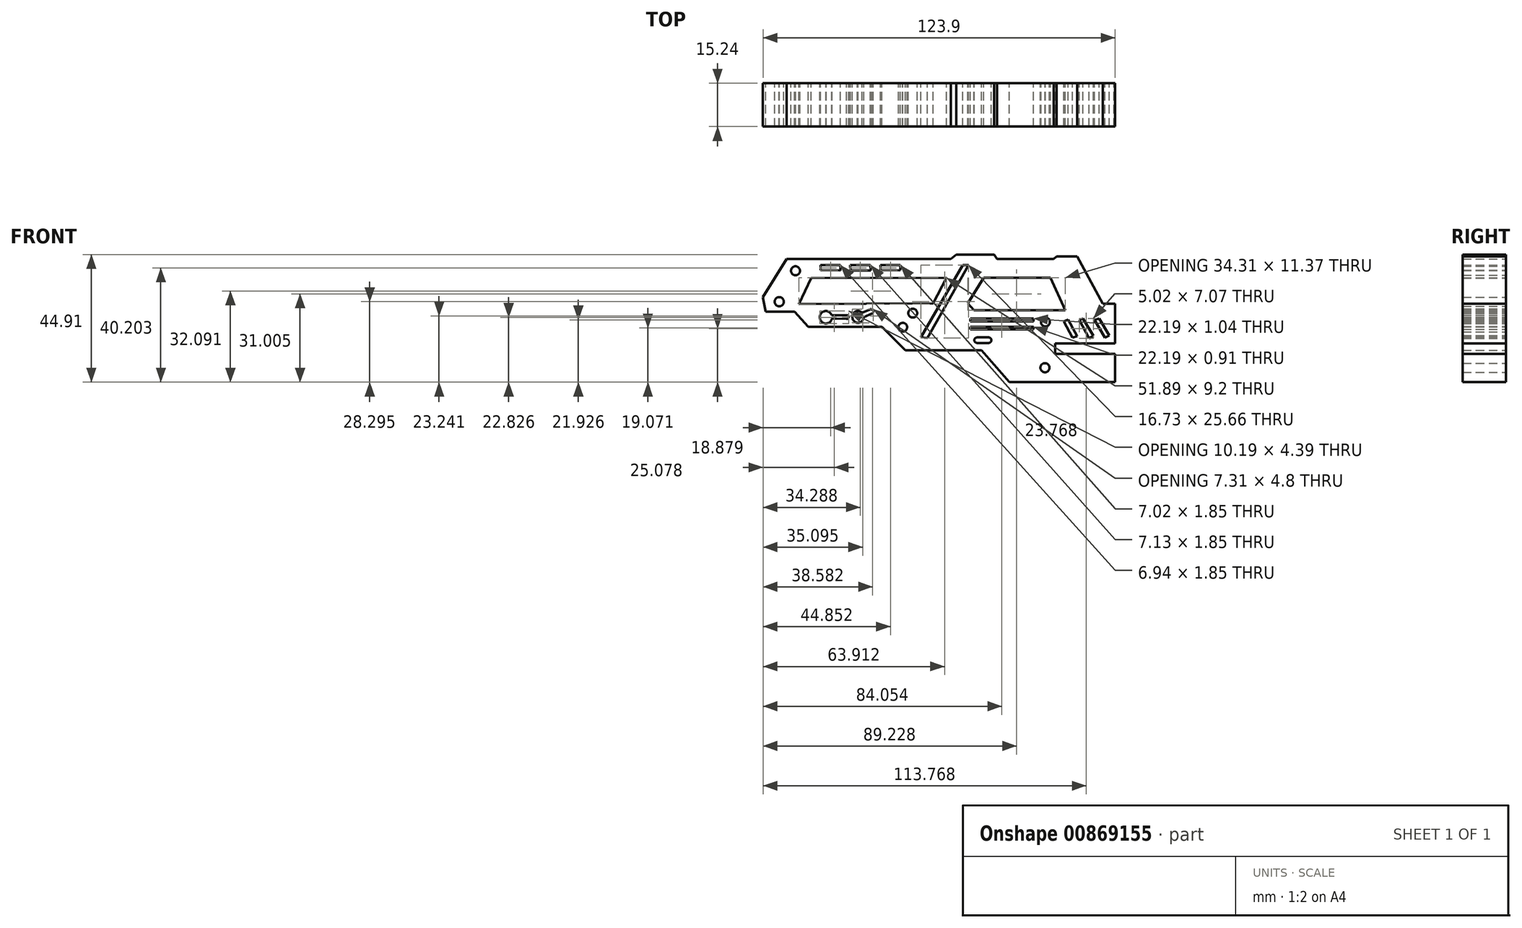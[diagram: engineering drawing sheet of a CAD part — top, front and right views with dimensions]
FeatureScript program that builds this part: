
annotation { "Feature Type Name" : "Feature", "Feature Type Description" : "" }
export const myFeature = defineFeature(function(context is Context, id is Id, definition is map)
    precondition{}
    {
        {
            var Q0;
            Q0=qCreatedBy(makeId("Front.planeOp"),FACE);
            var sketch = newSketch(context, id + "F0", { "sketchPlane" : qUnion([Q0])});
            skLineSegment(sketch, "E0", {"start": v(-62.2, 26.43) * mm, "end": v(-53.9, 39.85) * mm});
            skLineSegment(sketch, "E1", {"start": v(-53.9, 39.85) * mm, "end": v(3.91, 39.85) * mm});
            skLineSegment(sketch, "E2", {"start": v(3.91, 39.85) * mm, "end": v(5.84, 41.45) * mm});
            skLineSegment(sketch, "E3", {"start": v(5.84, 41.45) * mm, "end": v(19.17, 41.45) * mm});
            skLineSegment(sketch, "E4", {"start": v(19.17, 41.45) * mm, "end": v(20.2, 39.85) * mm});
            skLineSegment(sketch, "E5", {"start": v(20.2, 39.85) * mm, "end": v(40.17, 39.85) * mm});
            skLineSegment(sketch, "E6", {"start": v(40.17, 39.85) * mm, "end": v(41.14, 40.8) * mm});
            skLineSegment(sketch, "E7", {"start": v(41.14, 40.8) * mm, "end": v(48.3, 40.8) * mm});
            skLineSegment(sketch, "E8", {"start": v(48.3, 40.8) * mm, "end": v(57.4, 24.1) * mm});
            skLineSegment(sketch, "E9", {"start": v(61.7, 21.4) * mm, "end": v(61.7, 17.16) * mm});
            skLineSegment(sketch, "E10", {"start": v(61.7, 14.01) * mm, "end": v(61.7, 10.1) * mm});
            skLineSegment(sketch, "E11", {"start": v(61.7, 10.1) * mm, "end": v(31.32, 10.1) * mm});
            skArc(sketch, "E12", {"start": v(31.32, 10.1) * mm, "mid": v(29.48, 8.26) * mm, "end": v(31.32, 6.43) * mm});
            skLineSegment(sketch, "E13", {"start": v(31.32, 6.43) * mm, "end": v(61.34, 6.43) * mm});
            skLineSegment(sketch, "E14", {"start": v(61.34, 6.43) * mm, "end": v(61.34, 3.6) * mm});
            skLineSegment(sketch, "E15", {"start": v(61.7, 0) * mm, "end": v(61.7, -3.46) * mm});
            skLineSegment(sketch, "E16", {"start": v(61.7, -3.46) * mm, "end": v(24.42, -3.46) * mm});
            skLineSegment(sketch, "E17", {"start": v(24.42, -3.46) * mm, "end": v(14.7, 7.79) * mm});
            skLineSegment(sketch, "E18", {"start": v(14.7, 7.79) * mm, "end": v(-12.14, 7.79) * mm});
            skLineSegment(sketch, "E19", {"start": v(-12.14, 7.79) * mm, "end": v(-20.36, 16) * mm});
            skLineSegment(sketch, "E20", {"start": v(-20.36, 16) * mm, "end": v(-46.21, 16) * mm});
            skLineSegment(sketch, "E21", {"start": v(-46.21, 16) * mm, "end": v(-51.04, 21.3) * mm});
            skLineSegment(sketch, "E22", {"start": v(-51.04, 21.3) * mm, "end": v(-61.25, 21.3) * mm});
            skLineSegment(sketch, "E23", {"start": v(-61.25, 21.3) * mm, "end": v(-62.2, 26.43) * mm});
            skLineSegment(sketch, "E24", {"start": v(12.34, 25.63) * mm, "end": v(15.68, 30.57) * mm});
            skLineSegment(sketch, "E25", {"start": v(15.68, 30.57) * mm, "end": v(37.45, 30.57) * mm});
            skLineSegment(sketch, "E26", {"start": v(37.45, 30.57) * mm, "end": v(40.6, 24.3) * mm});
            skLineSegment(sketch, "E27", {"start": v(40.6, 24.3) * mm, "end": v(13.46, 24.3) * mm});
            skLineSegment(sketch, "E28", {"start": v(13.46, 24.3) * mm, "end": v(12.34, 25.63) * mm});
            skPoint(sketch, "E29.start.orphan", {"position": v(-49.56, 26.43) * mm});
            skPoint(sketch, "E30.start.orphan", {"position": v(-46.21, 33.1) * mm});
            skPoint(sketch, "E31.end.orphan", {"position": v(-49.56, 24.03) * mm});
            skLineSegment(sketch, "E32", {"start": v(-45.79, 27.78) * mm, "end": v(-43.34, 31.74) * mm});
            skLineSegment(sketch, "E33", {"start": v(-43.34, 31.74) * mm, "end": v(0, 31.74) * mm});
            skLineSegment(sketch, "E34", {"start": v(0, 31.74) * mm, "end": v(-2.07, 27.18) * mm});
            skLineSegment(sketch, "E35", {"start": v(-2.07, 27.18) * mm, "end": v(-45.79, 27.78) * mm});
            skPoint(sketch, "E36.start.orphan", {"position": v(59.67, 0) * mm});
            skLineSegment(sketch, "E37", {"start": v(61.7, 10.1) * mm, "end": v(61.7, 24.1) * mm});
            skLineSegment(sketch, "E38", {"start": v(61.7, 24.1) * mm, "end": v(57.4, 24.1) * mm});
            skLineSegment(sketch, "E39", {"start": v(57.4, 24.1) * mm, "end": v(61.7, 24.1) * mm});
            skLineSegment(sketch, "E40", {"start": v(-6.65, 12.26) * mm, "end": v(8.03, 37.67) * mm});
            skLineSegment(sketch, "E41", {"start": v(8.03, 37.67) * mm, "end": v(10.07, 37.67) * mm});
            skLineSegment(sketch, "E42", {"start": v(10.07, 37.67) * mm, "end": v(-4.35, 12) * mm});
            skLineSegment(sketch, "E43", {"start": v(-4.35, 12) * mm, "end": v(-6.65, 12.26) * mm});
            skLineSegment(sketch, "E44", {"start": v(-1.93, 12.26) * mm, "end": v(12.36, 37.67) * mm});
            skLineSegment(sketch, "E45", {"start": v(12.36, 37.67) * mm, "end": v(14.29, 37.67) * mm});
            skLineSegment(sketch, "E46", {"start": v(14.29, 37.67) * mm, "end": v(-0.14, 12) * mm});
            skLineSegment(sketch, "E47", {"start": v(-0.14, 12) * mm, "end": v(-1.96, 12.03) * mm});
            skLineSegment(sketch, "E48", {"start": v(10.76, 18.92) * mm, "end": v(10.76, 17.95) * mm});
            skLineSegment(sketch, "E49", {"start": v(10.76, 17.95) * mm, "end": v(32.95, 17.95) * mm});
            skLineSegment(sketch, "E50", {"start": v(32.95, 17.95) * mm, "end": v(32.95, 18.98) * mm});
            skLineSegment(sketch, "E51", {"start": v(32.95, 18.98) * mm, "end": v(10.76, 18.92) * mm});
            skLineSegment(sketch, "E52", {"start": v(10.76, 15.16) * mm, "end": v(32.95, 15.16) * mm});
            skLineSegment(sketch, "E53", {"start": v(32.95, 15.16) * mm, "end": v(32.95, 16.06) * mm});
            skLineSegment(sketch, "E54", {"start": v(32.95, 16.06) * mm, "end": v(10.76, 16.06) * mm});
            skLineSegment(sketch, "E55", {"start": v(10.76, 16.06) * mm, "end": v(10.76, 15.16) * mm});
            skLineSegment(sketch, "E56", {"start": v(35.6, 2.11) * mm, "end": v(35.6, 2.32) * mm});
            skLineSegment(sketch, "E57", {"start": v(-13.26, 8.9) * mm, "end": v(-4.35, 24.3) * mm});
            skLineSegment(sketch, "E58", {"start": v(-4.35, 24.3) * mm, "end": v(-2.07, 26.59) * mm});
            skLineSegment(sketch, "E59", {"start": v(40.6, -3.46) * mm, "end": v(40.6, 20.92) * mm});
            skLineSegment(sketch, "E60", {"start": v(40.6, 20.92) * mm, "end": v(39, 24.1) * mm});
            skLineSegment(sketch, "E61", {"start": v(28.58, 30.57) * mm, "end": v(28.58, 39.85) * mm});
            skLineSegment(sketch, "E62", {"start": v(1.26, 31.74) * mm, "end": v(1.26, 33.23) * mm});
            skLineSegment(sketch, "E63", {"start": v(1.26, 33.23) * mm, "end": v(5.08, 39.85) * mm});
            skLineSegment(sketch, "E64", {"start": v(5.08, 39.85) * mm, "end": v(5.84, 41.45) * mm});
            skLineSegment(sketch, "E65", {"start": v(-49.56, 24.03) * mm, "end": v(-2.3, 24.3) * mm});
            skLineSegment(sketch, "E66", {"start": v(-2.3, 24.3) * mm, "end": v(2.33, 33.23) * mm});
            skLineSegment(sketch, "E67", {"start": v(2.33, 33.23) * mm, "end": v(-45.19, 33.1) * mm});
            skLineSegment(sketch, "E68", {"start": v(-45.19, 33.1) * mm, "end": v(-49.56, 24.03) * mm});
            skLineSegment(sketch, "E69", {"start": v(9.87, 24.3) * mm, "end": v(11.98, 21.86) * mm});
            skLineSegment(sketch, "E70", {"start": v(11.98, 21.86) * mm, "end": v(44.18, 21.86) * mm});
            skLineSegment(sketch, "E71", {"start": v(44.18, 21.86) * mm, "end": v(39, 33.23) * mm});
            skLineSegment(sketch, "E72", {"start": v(39, 33.23) * mm, "end": v(15.47, 33.23) * mm});
            skLineSegment(sketch, "E73", {"start": v(15.47, 33.23) * mm, "end": v(9.87, 24.3) * mm});
            skLineSegment(sketch, "E74", {"start": v(-41.9, 35.92) * mm, "end": v(-41.9, 37.67) * mm});
            skLineSegment(sketch, "E75", {"start": v(-41.9, 37.67) * mm, "end": v(-34.97, 37.67) * mm});
            skLineSegment(sketch, "E76", {"start": v(-34.97, 37.67) * mm, "end": v(-34.96, 35.82) * mm});
            skLineSegment(sketch, "E77", {"start": v(-34.96, 35.82) * mm, "end": v(-41.9, 35.92) * mm});
            skLineSegment(sketch, "E78", {"start": v(-31.47, 35.82) * mm, "end": v(-31.48, 37.67) * mm});
            skLineSegment(sketch, "E79", {"start": v(-31.48, 37.67) * mm, "end": v(-24.36, 37.67) * mm});
            skLineSegment(sketch, "E80", {"start": v(-24.36, 37.67) * mm, "end": v(-24.35, 35.82) * mm});
            skLineSegment(sketch, "E81", {"start": v(-24.35, 35.82) * mm, "end": v(-31.47, 35.82) * mm});
            skLineSegment(sketch, "E82", {"start": v(-20.85, 35.82) * mm, "end": v(-20.86, 37.67) * mm});
            skLineSegment(sketch, "E83", {"start": v(-20.86, 37.67) * mm, "end": v(-13.84, 37.67) * mm});
            skLineSegment(sketch, "E84", {"start": v(-13.84, 37.67) * mm, "end": v(-13.84, 35.92) * mm});
            skLineSegment(sketch, "E85", {"start": v(-13.84, 35.92) * mm, "end": v(-20.85, 35.82) * mm});
            skLineSegment(sketch, "E86", {"start": v(-8.77, 39.85) * mm, "end": v(-8.76, 38.45) * mm});
            skLineSegment(sketch, "E87", {"start": v(-8.76, 38.45) * mm, "end": v(-1.27, 38.45) * mm});
            skLineSegment(sketch, "E88", {"start": v(-1.27, 38.45) * mm, "end": v(-1.28, 39.85) * mm});
            skLineSegment(sketch, "E89", {"start": v(-38, 20.4) * mm, "end": v(-38, 20.03) * mm});
            skPoint(sketch, "E90.start.orphan", {"position": v(-40.9, 21.11) * mm});
            skLineSegment(sketch, "E91", {"start": v(-42.17, 20.03) * mm, "end": v(-32.77, 20.03) * mm});
            skLineSegment(sketch, "E92", {"start": v(-42.16, 19) * mm, "end": v(-32.8, 18.83) * mm});
            skArc(sketch, "E93", {"start": v(-32.8, 18.83) * mm, "mid": v(-32.03, 19.4) * mm, "end": v(-32.77, 20.03) * mm});
            skLineSegment(sketch, "E94", {"start": v(43.6, 17.86) * mm, "end": v(46.74, 12.23) * mm});
            skLineSegment(sketch, "E95", {"start": v(46.74, 12.23) * mm, "end": v(48.4, 12.64) * mm});
            skLineSegment(sketch, "E96", {"start": v(48.4, 12.64) * mm, "end": v(45.12, 18.58) * mm});
            skLineSegment(sketch, "E97", {"start": v(45.12, 18.58) * mm, "end": v(43.6, 17.86) * mm});
            skLineSegment(sketch, "E98", {"start": v(49.06, 18.37) * mm, "end": v(50.38, 18.95) * mm});
            skLineSegment(sketch, "E99", {"start": v(50.38, 18.95) * mm, "end": v(54.08, 12.81) * mm});
            skLineSegment(sketch, "E100", {"start": v(54.08, 12.81) * mm, "end": v(52.54, 11.89) * mm});
            skLineSegment(sketch, "E101", {"start": v(52.54, 11.89) * mm, "end": v(49.06, 18.37) * mm});
            skLineSegment(sketch, "E102", {"start": v(54.44, 18.37) * mm, "end": v(58.18, 12.23) * mm});
            skLineSegment(sketch, "E103", {"start": v(58.18, 12.23) * mm, "end": v(59.7, 12.9) * mm});
            skLineSegment(sketch, "E104", {"start": v(59.7, 12.9) * mm, "end": v(56.15, 18.93) * mm});
            skLineSegment(sketch, "E105", {"start": v(56.15, 18.93) * mm, "end": v(54.44, 18.37) * mm});
            skLineSegment(sketch, "E106", {"start": v(61.6, 13.65) * mm, "end": v(59.95, 13.65) * mm});
            skLineSegment(sketch, "E107", {"start": v(59.95, 13.65) * mm, "end": v(59.93, 17.16) * mm});
            skLineSegment(sketch, "E108", {"start": v(59.93, 17.16) * mm, "end": v(61.7, 17.16) * mm});
            skLineSegment(sketch, "E109", {"start": v(61.7, -0.64) * mm, "end": v(61.7, 6.43) * mm});
            skLineSegment(sketch, "E110", {"start": v(61.7, 6.43) * mm, "end": v(61.34, 6.43) * mm});
            skLineSegment(sketch, "E111", {"start": v(61.7, 3.23) * mm, "end": v(59.7, 3.23) * mm});
            skLineSegment(sketch, "E112", {"start": v(59.7, 3.23) * mm, "end": v(59.72, -0.56) * mm});
            skLineSegment(sketch, "E113", {"start": v(59.72, -0.56) * mm, "end": v(61.7, -0.56) * mm});
            skLineSegment(sketch, "E114", {"start": v(55.3, -1.75) * mm, "end": v(42.91, -1.75) * mm});
            skLineSegment(sketch, "E115", {"start": v(42.91, -1.75) * mm, "end": v(42.91, 4.58) * mm});
            skLineSegment(sketch, "E116", {"start": v(42.91, 4.58) * mm, "end": v(55.3, 4.58) * mm});
            skLineSegment(sketch, "E117", {"start": v(55.3, 4.58) * mm, "end": v(55.3, 4.37) * mm});
            skLineSegment(sketch, "E118", {"start": v(41.14, 33.74) * mm, "end": v(46.43, 23.05) * mm});
            skLineSegment(sketch, "E119", {"start": v(55.78, 23.05) * mm, "end": v(47.72, 37.85) * mm});
            skArc(sketch, "E120", {"start": v(46.1, 33.68) * mm, "mid": v(47.87, 35.39) * mm, "end": v(47.72, 37.85) * mm});
            skLineSegment(sketch, "E121", {"start": v(41.14, 33.74) * mm, "end": v(46.1, 33.68) * mm});
            skLineSegment(sketch, "E122", {"start": v(15.82, 34.57) * mm, "end": v(27.34, 34.44) * mm});
            skLineSegment(sketch, "E123", {"start": v(27.34, 38.3) * mm, "end": v(18, 38.3) * mm});
            skLineSegment(sketch, "E124", {"start": v(18, 38.3) * mm, "end": v(15.82, 34.57) * mm});
            skLineSegment(sketch, "E125", {"start": v(17.21, 10.34) * mm, "end": v(13.11, 10.34) * mm});
            skArc(sketch, "E126", {"start": v(13.11, 12.26) * mm, "mid": v(12.15, 11.3) * mm, "end": v(13.11, 10.34) * mm});
            skLineSegment(sketch, "E127", {"start": v(13.11, 12.26) * mm, "end": v(17.21, 12.26) * mm});
            skArc(sketch, "E128", {"start": v(17.21, 10.34) * mm, "mid": v(18.17, 11.3) * mm, "end": v(17.21, 12.26) * mm});
            skLineSegment(sketch, "E129", {"start": v(21.11, 12.41) * mm, "end": v(25.16, 12.41) * mm});
            skArc(sketch, "E130", {"start": v(25.55, 10.44) * mm, "mid": v(26.17, 11.59) * mm, "end": v(25.16, 12.41) * mm});
            skLineSegment(sketch, "E131", {"start": v(21.4, 10.34) * mm, "end": v(25.55, 10.34) * mm});
            skArc(sketch, "E132", {"start": v(21.11, 12.41) * mm, "mid": v(20.36, 11.25) * mm, "end": v(21.4, 10.34) * mm});
            skLineSegment(sketch, "E133", {"start": v(-12.42, 30.15) * mm, "end": v(-3.9, 30.15) * mm});
            skArc(sketch, "E134", {"start": v(-3.9, 28.73) * mm, "mid": v(-3.18, 29.44) * mm, "end": v(-3.9, 30.15) * mm});
            skLineSegment(sketch, "E135", {"start": v(-12.4, 28.73) * mm, "end": v(-3.9, 28.73) * mm});
            skArc(sketch, "E136", {"start": v(-12.42, 30.15) * mm, "mid": v(-13.1, 29.43) * mm, "end": v(-12.4, 28.73) * mm});
            skArc(sketch, "E137", {"start": v(-28.99, 21.6) * mm, "mid": v(-30.76, 19.4) * mm, "end": v(-28.78, 17.38) * mm});
            skArc(sketch, "E138", {"start": v(-28.78, 17.38) * mm, "mid": v(-26.76, 19.6) * mm, "end": v(-28.99, 21.6) * mm});
            skLineSegment(sketch, "E139", {"start": v(-27.68, 20.81) * mm, "end": v(-24.6, 22.11) * mm});
            skArc(sketch, "E140", {"start": v(-23.74, 20.7) * mm, "mid": v(-23.56, 21.78) * mm, "end": v(-24.6, 22.11) * mm});
            skLineSegment(sketch, "E141", {"start": v(-23.74, 20.7) * mm, "end": v(-26.76, 19.39) * mm});
            skPoint(sketch, "E141.endSnap0", {"position": v(-26.76, 19.6) * mm});
            skArc(sketch, "E142", {"start": v(-27.68, 20.81) * mm, "mid": v(-27.82, 19.7) * mm, "end": v(-26.76, 19.39) * mm});
            skPoint(sketch, "E143.start.orphan", {"position": v(-40.9, 21.56) * mm});
            skPoint(sketch, "E144.start.orphan", {"position": v(-40.3, 21.56) * mm});
            skPoint(sketch, "E145.start.orphan", {"position": v(-38.4, 20.96) * mm});
            skLineSegment(sketch, "E146.trimOffspring", {"start": v(-37.99, 18.92) * mm, "end": v(-37.98, 18.45) * mm});
            skPoint(sketch, "E147.start.orphan", {"position": v(-38.4, 17.74) * mm});
            skPoint(sketch, "E148.end.orphan", {"position": v(-42.17, 18.45) * mm});
            skPoint(sketch, "E149.orphan", {"position": v(-42.17, 19.65) * mm});
            skPoint(sketch, "E150.end.orphan", {"position": v(-42.17, 20.4) * mm});
            skArc(sketch, "E151", {"start": v(-39.9, 21.56) * mm, "mid": v(-42.22, 19.45) * mm, "end": v(-40.07, 17.17) * mm});
            skArc(sketch, "E152", {"start": v(-40.07, 17.17) * mm, "mid": v(-37.9, 19.29) * mm, "end": v(-39.9, 21.56) * mm});
            skPoint(sketch, "E153.start.orphan", {"position": v(-56.55, 26.25) * mm});
            skPoint(sketch, "E154.start.orphan", {"position": v(-56.55, 23.5) * mm});
            skArc(sketch, "E155", {"start": v(-56.55, 26.48) * mm, "mid": v(-58.07, 24.76) * mm, "end": v(-56.38, 23.21) * mm});
            skArc(sketch, "E156", {"start": v(-56.38, 23.21) * mm, "mid": v(-54.86, 24.93) * mm, "end": v(-56.55, 26.48) * mm});
            skArc(sketch, "E157", {"start": v(-50.88, 37.3) * mm, "mid": v(-52.32, 35.63) * mm, "end": v(-50.72, 34.12) * mm});
            skArc(sketch, "E158", {"start": v(-50.72, 34.12) * mm, "mid": v(-49.18, 35.8) * mm, "end": v(-50.88, 37.3) * mm});
            skArc(sketch, "E159", {"start": v(-13.1, 17.43) * mm, "mid": v(-14.55, 15.82) * mm, "end": v(-13.03, 14.28) * mm});
            skArc(sketch, "E160", {"start": v(-13.03, 14.28) * mm, "mid": v(-11.48, 15.89) * mm, "end": v(-13.1, 17.43) * mm});
            skPoint(sketch, "E161.start.orphan", {"position": v(-8.1, 21.4) * mm});
            skPoint(sketch, "E162.start.orphan", {"position": v(-10.89, 21.4) * mm});
            skArc(sketch, "E163", {"start": v(-9.55, 22.37) * mm, "mid": v(-11.07, 20.74) * mm, "end": v(-9.41, 19.26) * mm});
            skArc(sketch, "E164", {"start": v(-9.41, 19.26) * mm, "mid": v(-7.94, 20.89) * mm, "end": v(-9.55, 22.37) * mm});
            skPoint(sketch, "E165.start.orphan", {"position": v(36.84, 3.23) * mm});
            skPoint(sketch, "E166.start.orphan", {"position": v(37.6, 3.23) * mm});
            skPoint(sketch, "E167.start.orphan", {"position": v(38.23, 2.87) * mm});
            skPoint(sketch, "E168.start.orphan", {"position": v(38.87, 2.11) * mm});
            skPoint(sketch, "E169.start.orphan", {"position": v(38.23, 0.97) * mm});
            skPoint(sketch, "E170.end.orphan", {"position": v(36.84, 0) * mm});
            skPoint(sketch, "E170.start.orphan", {"position": v(38.21, 0) * mm});
            skPoint(sketch, "E171.start.orphan", {"position": v(35.6, 0) * mm});
            skPoint(sketch, "E172.start.orphan", {"position": v(35.6, 0.97) * mm});
            skArc(sketch, "E173", {"start": v(37.06, 3.23) * mm, "mid": v(35.43, 1.6) * mm, "end": v(37.08, 0) * mm});
            skArc(sketch, "E174", {"start": v(37.08, 0) * mm, "mid": v(38.58, 1.62) * mm, "end": v(37.06, 3.23) * mm});
            skPoint(sketch, "E175.end.orphan", {"position": v(38.23, 18.98) * mm});
            skPoint(sketch, "E176.end.orphan", {"position": v(36.84, 19.76) * mm});
            skPoint(sketch, "E177.end.orphan", {"position": v(35.6, 18.92) * mm});
            skPoint(sketch, "E178.end.orphan", {"position": v(35.6, 17.95) * mm});
            skPoint(sketch, "E179.end.orphan", {"position": v(36.64, 16.6) * mm});
            skPoint(sketch, "E180.end.orphan", {"position": v(37.6, 16.06) * mm});
            skPoint(sketch, "E181.end.orphan", {"position": v(38.23, 16.6) * mm});
            skPoint(sketch, "E181.start.orphan", {"position": v(38.98, 17.95) * mm});
            skArc(sketch, "E182", {"start": v(37.08, 19.3) * mm, "mid": v(35.62, 17.63) * mm, "end": v(37.23, 16.1) * mm});
            skArc(sketch, "E183", {"start": v(37.23, 16.1) * mm, "mid": v(38.74, 17.77) * mm, "end": v(37.08, 19.3) * mm});
            skSolve(sketch);
        }
        {
            var Q0;
            Q0 = qSketchRegion(id + "F0", true);
            extrude(context, id + "F1", {"entities" : qUnion([Q0]), "depth" : 10.4 * mm, "offsetDistance" : 25.4 * mm});
        }
        {
            var Q0;
            Q0 = qSketchRegion(id + "F0", true);
            extrude(context, id + "F2", {"entities" : qUnion([Q0]), "operationType" : NewBodyOperationType.ADD, "depth" : 15 * mm, "offsetDistance" : 25.4 * mm});
        }
        {
            var Q0;
            Q0 = qSketchRegion(id + "F0", true);
            extrude(context, id + "F3", {"entities" : qUnion([Q0]), "operationType" : NewBodyOperationType.ADD, "depth" : 15.24 * mm, "offsetDistance" : 25.4 * mm});
        }
    });
